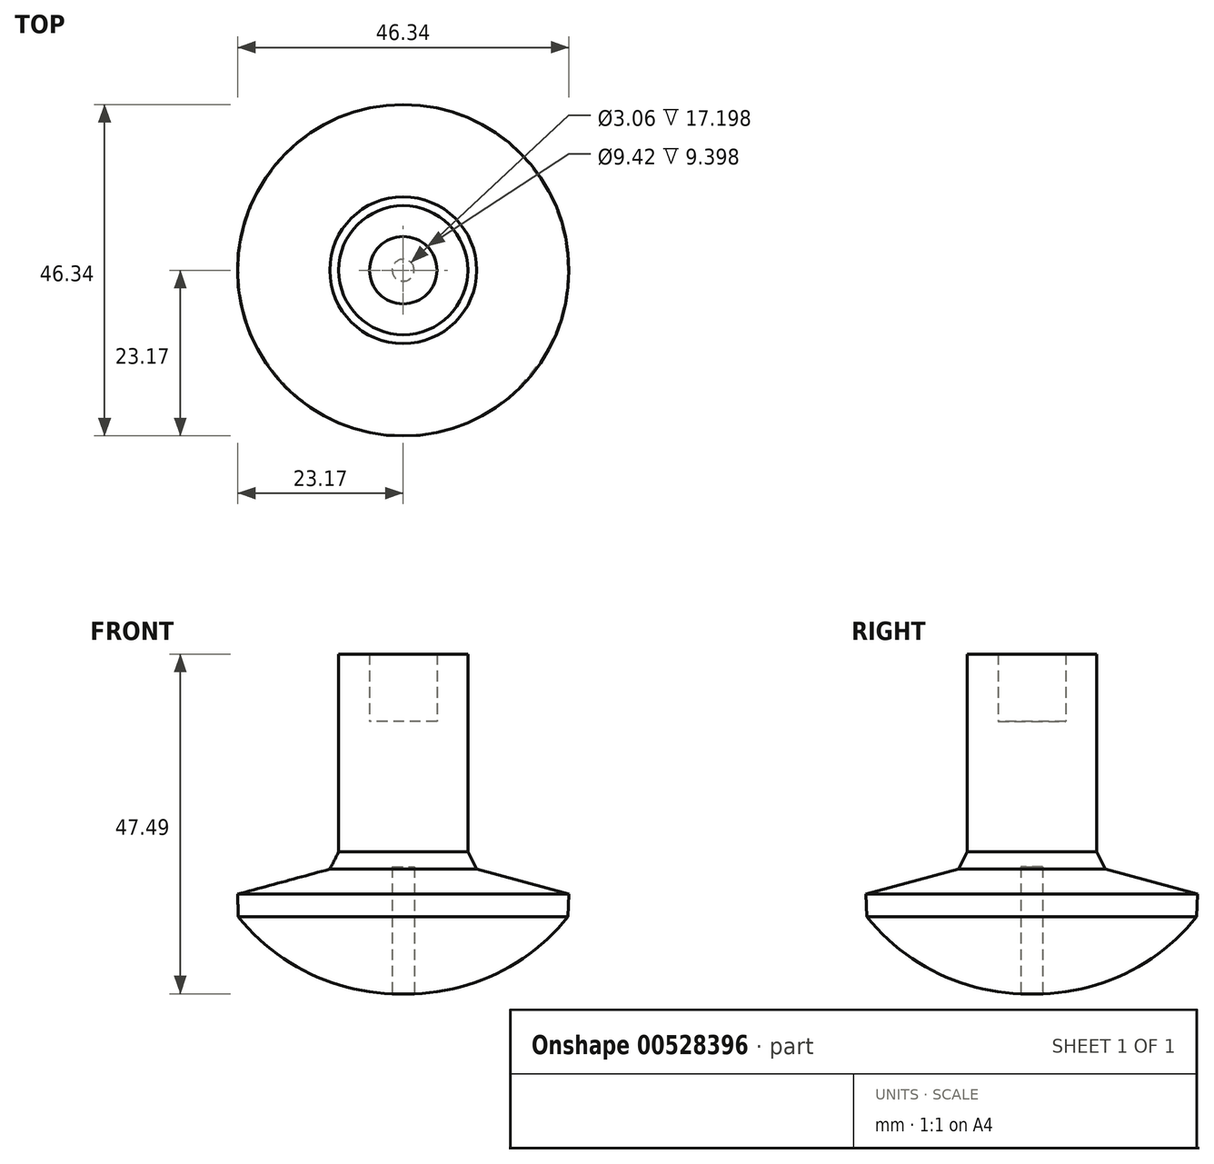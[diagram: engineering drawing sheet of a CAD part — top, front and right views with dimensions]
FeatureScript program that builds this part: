
annotation { "Feature Type Name" : "Feature", "Feature Type Description" : "" }
export const myFeature = defineFeature(function(context is Context, id is Id, definition is map)
    precondition{}
    {
        {
            var Q0;
            Q0=qCreatedBy(makeId("Front.planeOp"),FACE);
            var sketch = newSketch(context, id + "F0", { "sketchPlane" : qUnion([Q0])});
            skLineSegment(sketch, "E0", {"start": v(0, 38.13) * mm, "end": v(5.05, 38.13) * mm});
            skPoint(sketch, "E1.endSnap0", {"position": v(31.72, 0) * mm});
            skLineSegment(sketch, "E2", {"start": v(10.26, 17.46) * mm, "end": v(23.17, 13.96) * mm});
            skLineSegment(sketch, "E3", {"start": v(23.04, 10.82) * mm, "end": v(23.17, 13.96) * mm});
            skLineSegment(sketch, "E4", {"start": v(0, 17.77) * mm, "end": v(1.53, 17.77) * mm});
            skLineSegment(sketch, "E5", {"start": v(1.53, 17.77) * mm, "end": v(1.53, 0.57) * mm});
            skLineSegment(sketch, "E6", {"start": v(1.53, 0.57) * mm, "end": v(1.53, 0.04) * mm});
            skArc(sketch, "E7", {"start": v(1.53, 0.04) * mm, "mid": v(13.47, 3.07) * mm, "end": v(23.04, 10.82) * mm});
            skLineSegment(sketch, "E8", {"start": v(5.05, 38.13) * mm, "end": v(9.03, 38.13) * mm});
            skLineSegment(sketch, "E9", {"start": v(9.03, 38.13) * mm, "end": v(9.03, 19.89) * mm});
            skLineSegment(sketch, "E10", {"start": v(10.26, 17.46) * mm, "end": v(9.03, 19.89) * mm});
            skLineSegment(sketch, "E11", {"start": v(0, 0) * mm, "end": v(0, 47.4) * mm});
            skSolve(sketch);
        }
        {
            var Q0;
            Q0=qSketchRegion(id+"F0",true);
            var Q1;
            Q1=sQuery(id+"F0.wireOp",EDGE,"E11");
            revolve(context, id + "F1", {"entities" : qUnion([Q0]), "axis" : qUnion([Q1]), "revolveType" : RevolveType.FULL});
        }
        {
            var Q0;
            Q0=makeQuery(id+"F1.opRevolve","SWEPT_FACE",FACE,{"disambiguationData":[OSD([sQuery(id+"F0.wireOp",EDGE,"E0"),sQuery(id+"F0.wireOp",EDGE,"E8")])]});
            var sketch = newSketch(context, id + "F2", { "sketchPlane" : qUnion([Q0])});
            skCircle(sketch, "E12", {"center": v(0, 0) * mm, "radius": 4.71 * mm});
            skSolve(sketch);
        }
        {
            var Q0;
            Q0=makeQuery(id+"F2.imprint","IMPRINT",FACE,{"disambiguationData":[TD([[makeQuery(id+"F2.imprint","IMPRINT",EDGE,{"derivedFrom":sQuery(id+"F2.wireOp",EDGE,"E12")}),-1.0]])]});
            extrude(context, id + "F3", {"entities" : qUnion([Q0]), "operationType" : NewBodyOperationType.ADD, "depth" : 9.4 * mm, "offsetDistance" : 25.4 * mm});
        }
    });
